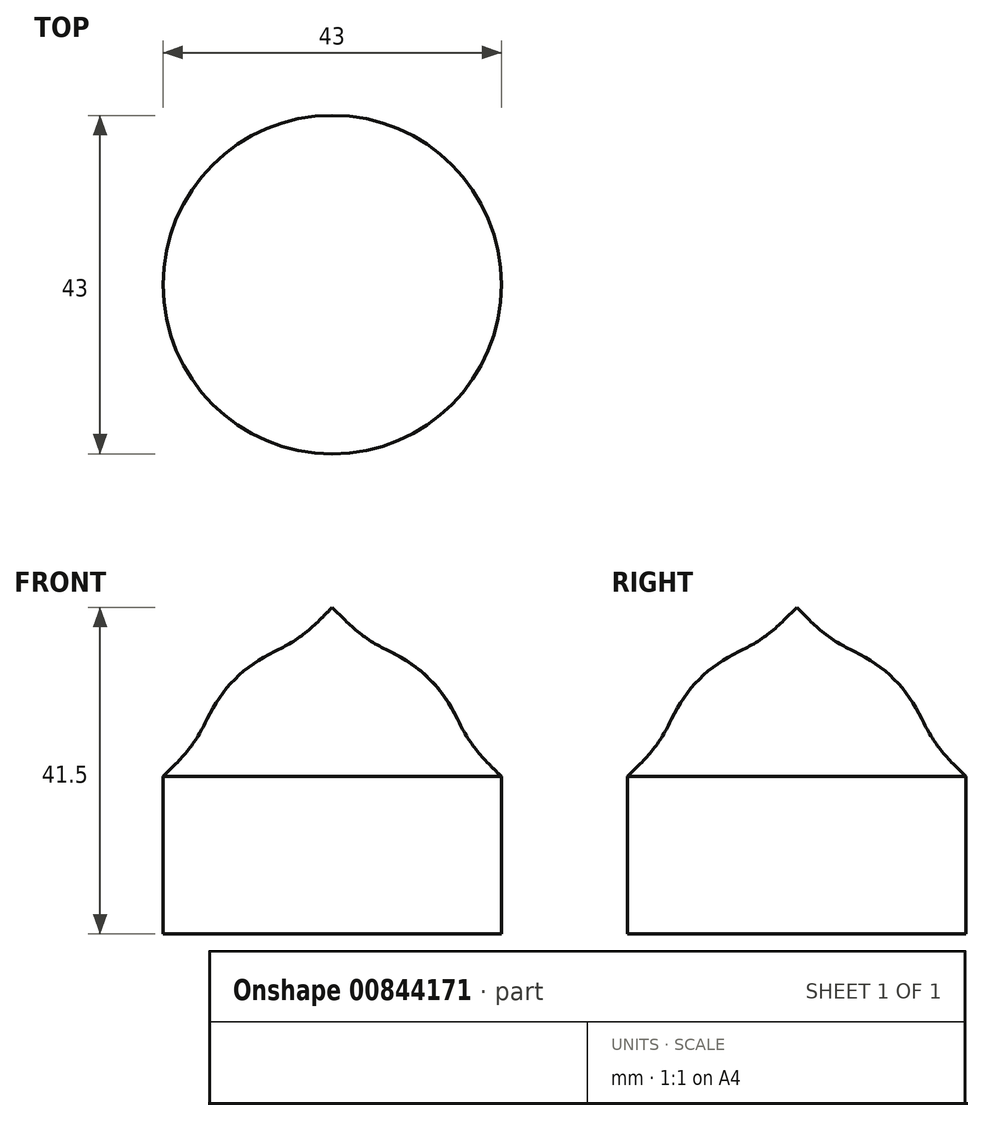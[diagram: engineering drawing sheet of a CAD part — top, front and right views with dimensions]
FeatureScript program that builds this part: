
annotation { "Feature Type Name" : "Feature", "Feature Type Description" : "" }
export const myFeature = defineFeature(function(context is Context, id is Id, definition is map)
    precondition{}
    {
        {
            var Q0;
            Q0=qCreatedBy(makeId("Front.planeOp"),FACE);
            var sketch = newSketch(context, id + "F0", { "sketchPlane" : qUnion([Q0])});
            skLineSegment(sketch, "E0", {"start": v(-21.5, 0) * mm, "end": v(0, 0) * mm});
            skLineSegment(sketch, "E1.left", {"start": v(-21.5, 0) * mm, "end": v(-21.5, 20) * mm});
            skArc(sketch, "E2", {"start": v(-7.35, 35.88) * mm, "mid": v(-12.37, 32.37) * mm, "end": v(-15.88, 27.35) * mm});
            skLineSegment(sketch, "E3", {"start": v(0, 41.5) * mm, "end": v(-1.61, 39.89) * mm});
            skLineSegment(sketch, "E4.trimOffspring", {"start": v(-19.89, 21.61) * mm, "end": v(-21.5, 20) * mm});
            skLineSegment(sketch, "E5", {"start": v(0, 41.5) * mm, "end": v(0, 0) * mm});
            skPoint(sketch, "E6.visualSharp", {"position": v(-4.62, 36.88) * mm});
            skArc(sketch, "E6.filletArc", {"start": v(-7.35, 35.88) * mm, "mid": v(-4.3, 37.63) * mm, "end": v(-1.61, 39.89) * mm});
            skPoint(sketch, "E7.visualSharp", {"position": v(-16.88, 24.62) * mm});
            skArc(sketch, "E7.filletArc", {"start": v(-19.89, 21.61) * mm, "mid": v(-17.63, 24.3) * mm, "end": v(-15.88, 27.35) * mm});
            skPoint(sketch, "E1.right.end.orphan", {"position": v(21.5, 20) * mm});
            skPoint(sketch, "E8.orphan", {"position": v(21.5, 0) * mm});
            skSolve(sketch);
        }
        {
            var Q0;
            Q0 = qSketchRegion(id + "F0", true);
            var Q1;
            Q1=sQuery(id+"F0.wireOp",EDGE,"E5");
            revolve(context, id + "F1", {"surfaceOperationType" : NewSurfaceOperationType.NEW, "entities" : qUnion([Q0]), "axis" : qUnion([Q1]), "revolveType" : RevolveType.FULL});
        }
    });
